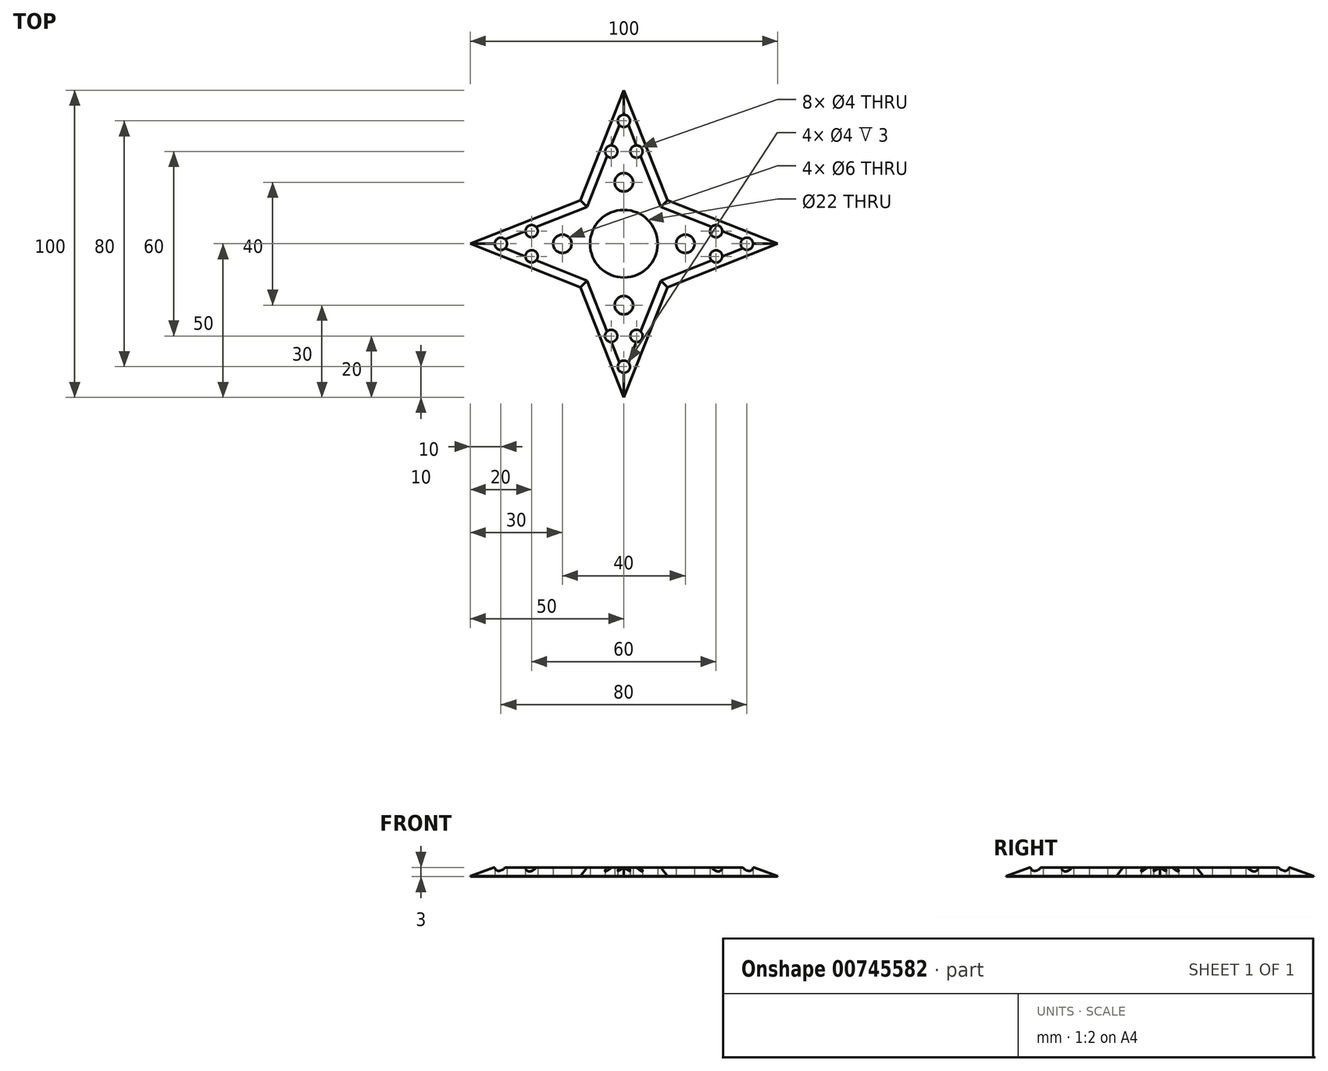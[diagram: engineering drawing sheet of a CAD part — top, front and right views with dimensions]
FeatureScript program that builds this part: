
annotation { "Feature Type Name" : "Feature", "Feature Type Description" : "" }
export const myFeature = defineFeature(function(context is Context, id is Id, definition is map)
    precondition{}
    {
        {
            var Q0;
            Q0=qCreatedBy(makeId("Top.planeOp"),FACE);
            var sketch = newSketch(context, id + "F0", { "sketchPlane" : qUnion([Q0])});
            skLineSegment(sketch, "E0", {"start": v(-50, 0) * mm, "end": v(-14.14, 14.14) * mm});
            skLineSegment(sketch, "E1", {"start": v(-14.14, -14.14) * mm, "end": v(-50, 0) * mm});
            skCircle(sketch, "E2", {"center": v(0, 0) * mm, "radius": 11 * mm});
            skCircle(sketch, "E3", {"center": v(-20, 0) * mm, "radius": 3 * mm});
            skPoint(sketch, "E4", {"position": v(-25, 0) * mm});
            skCircle(sketch, "E5", {"center": v(-30, 4.12) * mm, "radius": 2 * mm});
            skCircle(sketch, "E6", {"center": v(-30, -4.1) * mm, "radius": 2 * mm});
            skCircle(sketch, "E7", {"center": v(-40, 0) * mm, "radius": 2 * mm});
            skPoint(sketch, "E8.3.8", {"position": v(-14.14, -14.14) * mm});
            skPoint(sketch, "E9.orphan", {"position": v(-30, 0) * mm});
            skPoint(sketch, "E10.1.0", {"position": v(14.14, -14.14) * mm});
            skCircle(sketch, "E10.1.2", {"center": v(0, -20) * mm, "radius": 3 * mm});
            skPoint(sketch, "E10.1.3", {"position": v(0, -30) * mm});
            skPoint(sketch, "E10.1.4", {"position": v(0, -25) * mm});
            skCircle(sketch, "E10.1.7", {"center": v(4.1, -30) * mm, "radius": 2 * mm});
            skCircle(sketch, "E10.1.8", {"center": v(0, -40) * mm, "radius": 2 * mm});
            skCircle(sketch, "E10.1.10", {"center": v(-4.12, -30) * mm, "radius": 2 * mm});
            skLineSegment(sketch, "E10.1.13", {"start": v(14.14, -14.14) * mm, "end": v(0, -50) * mm});
            skLineSegment(sketch, "E10.1.14", {"start": v(0, -50) * mm, "end": v(-14.14, -14.14) * mm});
            skPoint(sketch, "E10.2.0", {"position": v(14.14, 14.14) * mm});
            skCircle(sketch, "E10.2.2", {"center": v(20, 0) * mm, "radius": 3 * mm});
            skPoint(sketch, "E10.2.3", {"position": v(30, 0) * mm});
            skPoint(sketch, "E10.2.4", {"position": v(25, 0) * mm});
            skCircle(sketch, "E10.2.7", {"center": v(30, 4.1) * mm, "radius": 2 * mm});
            skCircle(sketch, "E10.2.8", {"center": v(40, 0) * mm, "radius": 2 * mm});
            skCircle(sketch, "E10.2.10", {"center": v(30, -4.12) * mm, "radius": 2 * mm});
            skLineSegment(sketch, "E10.2.13", {"start": v(14.14, 14.14) * mm, "end": v(50, 0) * mm});
            skLineSegment(sketch, "E10.2.14", {"start": v(50, 0) * mm, "end": v(14.14, -14.14) * mm});
            skPoint(sketch, "E10.3.0", {"position": v(-14.14, 14.14) * mm});
            skCircle(sketch, "E10.3.2", {"center": v(0, 20) * mm, "radius": 3 * mm});
            skPoint(sketch, "E10.3.3", {"position": v(0, 30) * mm});
            skPoint(sketch, "E10.3.4", {"position": v(0, 25) * mm});
            skCircle(sketch, "E10.3.7", {"center": v(-4.1, 30) * mm, "radius": 2 * mm});
            skCircle(sketch, "E10.3.8", {"center": v(0, 40) * mm, "radius": 2 * mm});
            skCircle(sketch, "E10.3.10", {"center": v(4.12, 30) * mm, "radius": 2 * mm});
            skLineSegment(sketch, "E10.3.13", {"start": v(-14.14, 14.14) * mm, "end": v(0, 50) * mm});
            skLineSegment(sketch, "E10.3.14", {"start": v(0, 50) * mm, "end": v(14.14, 14.14) * mm});
            skSolve(sketch);
        }
        {
            var Q0;
            Q0 = qSketchRegion(id + "F0", true);
            extrude(context, id + "F1", {"entities" : qUnion([Q0]), "depth" : 3 * mm, "offsetDistance" : 25 * mm});
        }
        {
            var Q0;
            Q0=makeQuery(id+"F1.opExtrude","CAP_EDGE",EDGE,{"disambiguationData":[OSD([sQuery(id+"F0.wireOp",EDGE,"E10.1.13")])],"isStart":false});
            chamfer(context, id + "F2", {"entities" : qUnion([Q0]), "width" : 2.8 * mm, "tangentPropagation" : true});
        }
        {
            var Q0;
            Q0=makeQuery(id+"F1.opExtrude","CAP_EDGE",EDGE,{"disambiguationData":[OSD([sQuery(id+"F0.wireOp",EDGE,"E10.1.14")])],"isStart":false});
            chamfer(context, id + "F3", {"entities" : qUnion([Q0]), "width" : 2.8 * mm, "tangentPropagation" : true});
        }
        {
            var Q0;
            Q0=makeQuery(id+"F1.opExtrude","CAP_EDGE",EDGE,{"disambiguationData":[OSD([sQuery(id+"F0.wireOp",EDGE,"E10.2.14")])],"isStart":false});
            var Q1;
            Q1=makeQuery(id+"F1.opExtrude","CAP_EDGE",EDGE,{"disambiguationData":[OSD([sQuery(id+"F0.wireOp",EDGE,"E10.2.13")])],"isStart":false});
            var Q2;
            Q2=makeQuery(id+"F1.opExtrude","CAP_EDGE",EDGE,{"disambiguationData":[OSD([sQuery(id+"F0.wireOp",EDGE,"E10.3.14")])],"isStart":false});
            var Q3;
            Q3=makeQuery(id+"F1.opExtrude","CAP_EDGE",EDGE,{"disambiguationData":[OSD([sQuery(id+"F0.wireOp",EDGE,"E1")])],"isStart":false});
            var Q4;
            Q4=makeQuery(id+"F1.opExtrude","CAP_EDGE",EDGE,{"disambiguationData":[OSD([sQuery(id+"F0.wireOp",EDGE,"E0")])],"isStart":false});
            var Q5;
            Q5=makeQuery(id+"F1.opExtrude","CAP_EDGE",EDGE,{"disambiguationData":[OSD([sQuery(id+"F0.wireOp",EDGE,"E10.3.13")])],"isStart":false});
            chamfer(context, id + "F4", {"entities" : qUnion([Q0, Q1, Q2, Q3, Q4, Q5]), "width" : 2.8 * mm, "tangentPropagation" : true});
        }
    });
